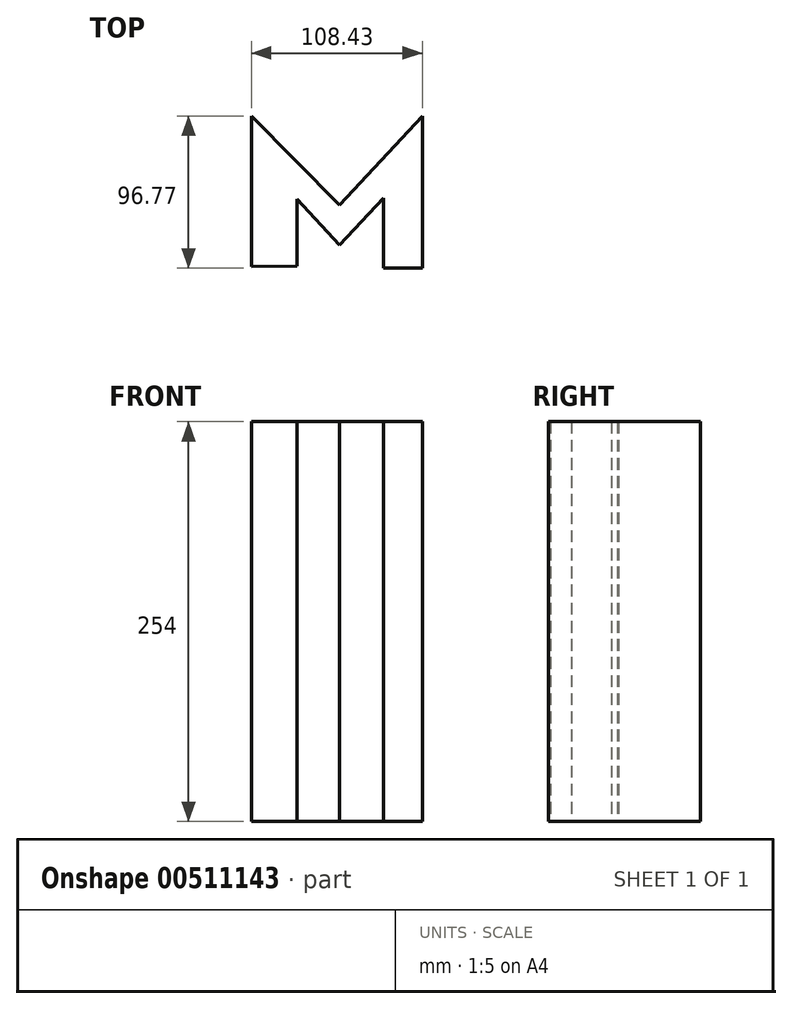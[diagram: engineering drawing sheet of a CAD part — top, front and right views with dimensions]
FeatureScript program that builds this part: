
annotation { "Feature Type Name" : "Feature", "Feature Type Description" : "" }
export const myFeature = defineFeature(function(context is Context, id is Id, definition is map)
    precondition{}
    {
        {
            var Q0;
            Q0=qCreatedBy(makeId("Top.planeOp"),FACE);
            var sketch = newSketch(context, id + "F0", { "sketchPlane" : qUnion([Q0])});
            skLineSegment(sketch, "E0", {"start": v(-55.96, -54.94) * mm, "end": v(-55.96, 40.66) * mm});
            skLineSegment(sketch, "E1", {"start": v(-55.96, 40.66) * mm, "end": v(0, -15.9) * mm});
            skLineSegment(sketch, "E2", {"start": v(0, -15.9) * mm, "end": v(52.47, 40.66) * mm});
            skLineSegment(sketch, "E3", {"start": v(52.47, 40.66) * mm, "end": v(52.47, -56.1) * mm});
            skLineSegment(sketch, "E4", {"start": v(52.47, -56.1) * mm, "end": v(27.75, -56.1) * mm});
            skLineSegment(sketch, "E5", {"start": v(27.75, -56.1) * mm, "end": v(27.75, -11.05) * mm});
            skLineSegment(sketch, "E6", {"start": v(27.87, -11.49) * mm, "end": v(0, -41.53) * mm});
            skLineSegment(sketch, "E7", {"start": v(0, -41.53) * mm, "end": v(-27.08, -12.2) * mm});
            skLineSegment(sketch, "E8", {"start": v(-27.08, -12.2) * mm, "end": v(-27.08, -54.6) * mm});
            skLineSegment(sketch, "E9", {"start": v(-27.08, -54.6) * mm, "end": v(-55.96, -54.94) * mm});
            skSolve(sketch);
        }
        {
            var Q0;
            Q0=makeQuery(id+"F0.imprint","IMPRINT",FACE,{"disambiguationData":[TD([[makeQuery(id+"F0.imprint","IMPRINT",EDGE,{"derivedFrom":sQuery(id+"F0.wireOp",EDGE,"E0")}),-1.0]])]});
            extrude(context, id + "F1", {"entities" : qUnion([Q0]), "depth" : 254 * mm});
        }
    });
